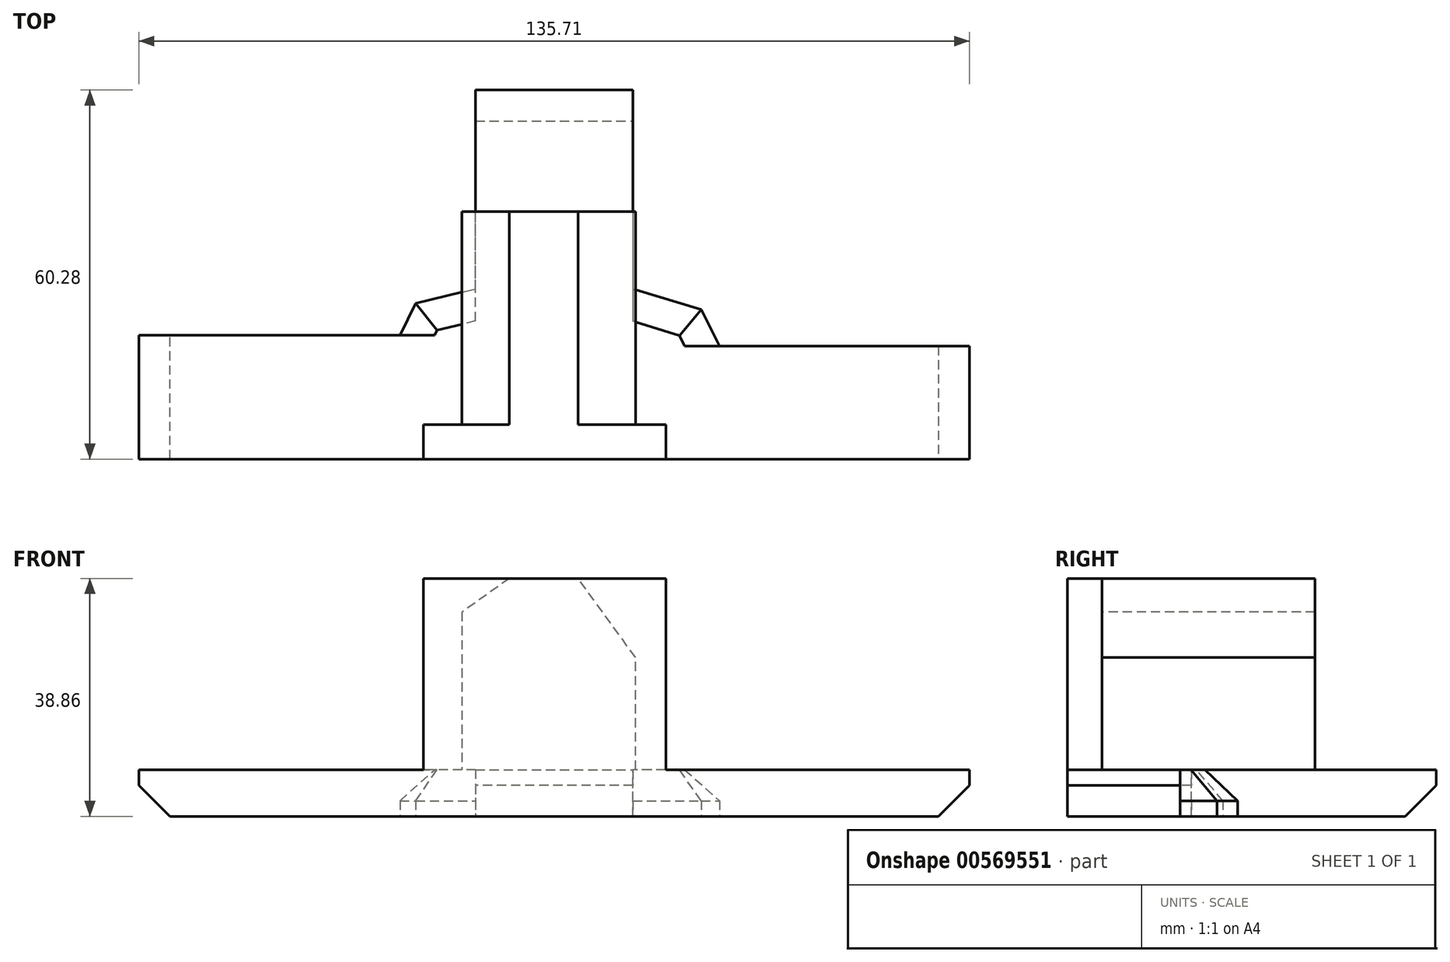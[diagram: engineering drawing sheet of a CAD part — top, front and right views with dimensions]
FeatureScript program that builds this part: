
annotation { "Feature Type Name" : "Feature", "Feature Type Description" : "" }
export const myFeature = defineFeature(function(context is Context, id is Id, definition is map)
    precondition{}
    {
        {
            var Q0;
            Q0=qCreatedBy(makeId("Top.planeOp"),FACE);
            var sketch = newSketch(context, id + "F0", { "sketchPlane" : qUnion([Q0])});
            skLineSegment(sketch, "E0", {"start": v(-76.52, 0) * mm, "end": v(-76.52, 20.23) * mm});
            skLineSegment(sketch, "E1", {"start": v(-76.52, 20.23) * mm, "end": v(-33.88, 20.23) * mm});
            skLineSegment(sketch, "E2", {"start": v(-33.88, 20.23) * mm, "end": v(-31.29, 25.4) * mm});
            skLineSegment(sketch, "E3", {"start": v(-31.29, 25.4) * mm, "end": v(-21.52, 27.8) * mm});
            skLineSegment(sketch, "E4", {"start": v(-21.52, 27.8) * mm, "end": v(-21.52, 60.28) * mm});
            skLineSegment(sketch, "E5", {"start": v(-21.52, 60.28) * mm, "end": v(4.18, 60.28) * mm});
            skLineSegment(sketch, "E6", {"start": v(4.18, 60.28) * mm, "end": v(4.18, 27.8) * mm});
            skLineSegment(sketch, "E7", {"start": v(4.18, 27.8) * mm, "end": v(15.34, 24.41) * mm});
            skLineSegment(sketch, "E8", {"start": v(15.34, 24.41) * mm, "end": v(18.33, 18.43) * mm});
            skLineSegment(sketch, "E9", {"start": v(18.33, 18.43) * mm, "end": v(59.19, 18.43) * mm});
            skLineSegment(sketch, "E10", {"start": v(59.19, 18.43) * mm, "end": v(59.19, 0) * mm});
            skLineSegment(sketch, "E11", {"start": v(59.19, 0) * mm, "end": v(-76.52, 0) * mm});
            skSolve(sketch);
        }
        {
            var Q0;
            Q0 = qSketchRegion(id + "F0", true);
            extrude(context, id + "F1", {"entities" : qUnion([Q0]), "depth" : 7.62 * mm, "offsetDistance" : 25.4 * mm});
        }
        {
            var Q0;
            Q0=makeQuery(id+"F1.opExtrude","CAP_EDGE",EDGE,{"disambiguationData":[OSD([sQuery(id+"F0.wireOp",EDGE,"E3")])],"isStart":false});
            var Q1;
            Q1=makeQuery(id+"F1.opExtrude","CAP_EDGE",EDGE,{"disambiguationData":[OSD([sQuery(id+"F0.wireOp",EDGE,"E2")])],"isStart":false});
            var Q2;
            Q2=makeQuery(id+"F1.opExtrude","CAP_EDGE",EDGE,{"disambiguationData":[OSD([sQuery(id+"F0.wireOp",EDGE,"E7")])],"isStart":false});
            var Q3;
            Q3=makeQuery(id+"F1.opExtrude","CAP_EDGE",EDGE,{"disambiguationData":[OSD([sQuery(id+"F0.wireOp",EDGE,"E8")])],"isStart":false});
            var Q4;
            Q4=makeQuery(id+"F1.opExtrude","CAP_EDGE",EDGE,{"disambiguationData":[OSD([sQuery(id+"F0.wireOp",EDGE,"E10")])],"isStart":true});
            var Q5;
            Q5=makeQuery(id+"F1.opExtrude","CAP_EDGE",EDGE,{"disambiguationData":[OSD([sQuery(id+"F0.wireOp",EDGE,"E0")])],"isStart":true});
            var Q6;
            Q6=makeQuery(id+"F1.opExtrude","CAP_EDGE",EDGE,{"disambiguationData":[OSD([sQuery(id+"F0.wireOp",EDGE,"E5")])],"isStart":true});
            chamfer(context, id + "F2", {"entities" : qUnion([Q0, Q1, Q2, Q3, Q4, Q5, Q6]), "width" : 5.08 * mm, "tangentPropagation" : true});
        }
        {
            var Q0;
            Q0=makeQuery(id+"F1.opExtrude","CAP_FACE",FACE,{"disambiguationData":[OSD([sQuery(id+"F0.wireOp",EDGE,"E0"),sQuery(id+"F0.wireOp",EDGE,"E1"),sQuery(id+"F0.wireOp",EDGE,"E2"),sQuery(id+"F0.wireOp",EDGE,"E3"),sQuery(id+"F0.wireOp",EDGE,"E4"),sQuery(id+"F0.wireOp",EDGE,"E5"),sQuery(id+"F0.wireOp",EDGE,"E6"),sQuery(id+"F0.wireOp",EDGE,"E7"),sQuery(id+"F0.wireOp",EDGE,"E8"),sQuery(id+"F0.wireOp",EDGE,"E9"),sQuery(id+"F0.wireOp",EDGE,"E10"),sQuery(id+"F0.wireOp",EDGE,"E11")])],"isStart":false});
            var sketch = newSketch(context, id + "F3", { "sketchPlane" : qUnion([Q0])});
            skLineSegment(sketch, "E12", {"start": v(9.57, 0) * mm, "end": v(9.57, 5.63) * mm});
            skLineSegment(sketch, "E13", {"start": v(9.57, 5.63) * mm, "end": v(-30.02, 5.63) * mm});
            skLineSegment(sketch, "E14", {"start": v(-30.02, 5.63) * mm, "end": v(-30.02, 0) * mm});
            skLineSegment(sketch, "E15", {"start": v(-30.02, 0) * mm, "end": v(9.57, 0) * mm});
            skSolve(sketch);
        }
        {
            var Q0;
            Q0 = qSketchRegion(id + "F3", true);
            extrude(context, id + "F4", {"entities" : qUnion([Q0]), "operationType" : NewBodyOperationType.ADD, "depth" : 31.24 * mm, "offsetDistance" : 25.4 * mm});
        }
        {
            var Q0;
            Q0=makeQuery(id+"F4.opExtrude","SWEPT_FACE",FACE,{"disambiguationData":[OSD([sQuery(id+"F3.wireOp",EDGE,"E13")])]});
            var sketch = newSketch(context, id + "F5", { "sketchPlane" : qUnion([Q0])});
            skLineSegment(sketch, "E16", {"start": v(-4.62, 7.62) * mm, "end": v(-4.62, 25.95) * mm});
            skLineSegment(sketch, "E17", {"start": v(-4.62, 25.95) * mm, "end": v(4.76, 38.86) * mm});
            skLineSegment(sketch, "E18", {"start": v(4.76, 38.86) * mm, "end": v(16, 38.86) * mm});
            skLineSegment(sketch, "E19", {"start": v(16, 38.86) * mm, "end": v(23.72, 33.36) * mm});
            skLineSegment(sketch, "E20", {"start": v(23.72, 33.36) * mm, "end": v(23.72, 7.62) * mm});
            skLineSegment(sketch, "E21", {"start": v(23.72, 7.62) * mm, "end": v(-4.62, 7.62) * mm});
            skLineSegment(sketch, "E22", {"start": v(4.76, 29.35) * mm, "end": v(16, 29.35) * mm});
            skLineSegment(sketch, "E23", {"start": v(16, 29.35) * mm, "end": v(19.88, 25.95) * mm});
            skLineSegment(sketch, "E24", {"start": v(19.88, 25.95) * mm, "end": v(19.88, 7.62) * mm});
            skLineSegment(sketch, "E25", {"start": v(19.88, 7.62) * mm, "end": v(0, 7.62) * mm});
            skLineSegment(sketch, "E26", {"start": v(0, 7.62) * mm, "end": v(0, 23.02) * mm});
            skLineSegment(sketch, "E27", {"start": v(0, 23.02) * mm, "end": v(4.76, 29.35) * mm});
            skSolve(sketch);
        }
        {
            var Q0;
            Q0 = qSketchRegion(id + "F5", true);
            extrude(context, id + "F6", {"entities" : qUnion([Q0]), "operationType" : NewBodyOperationType.ADD, "depth" : 34.8 * mm, "offsetDistance" : 25.4 * mm});
        }
    });
